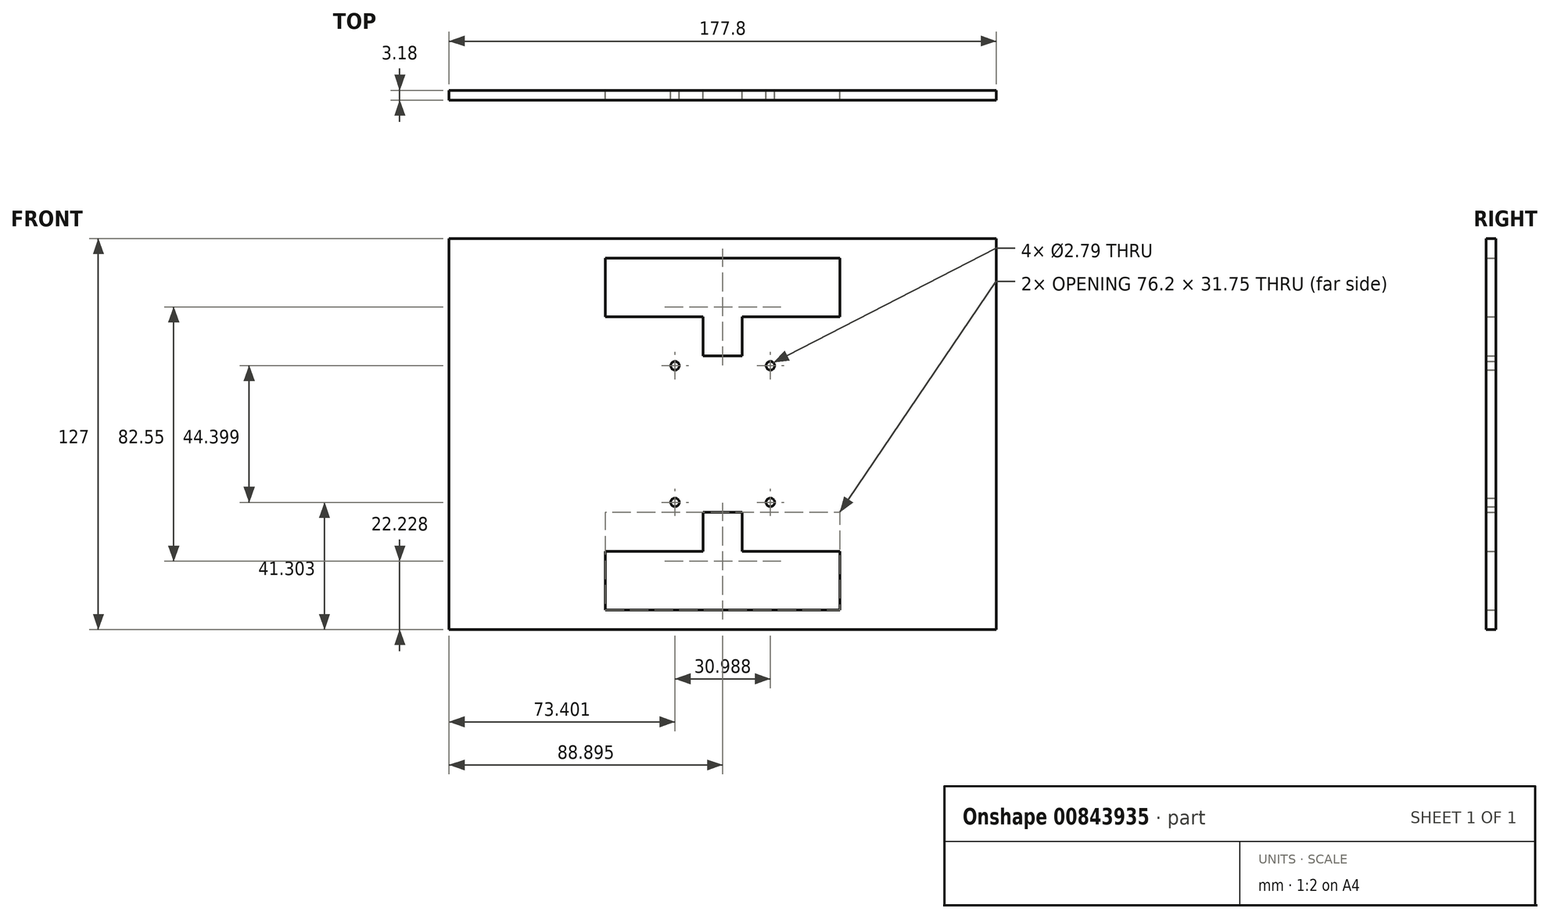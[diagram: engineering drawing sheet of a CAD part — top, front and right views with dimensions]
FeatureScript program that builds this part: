
annotation { "Feature Type Name" : "Feature", "Feature Type Description" : "" }
export const myFeature = defineFeature(function(context is Context, id is Id, definition is map)
    precondition{}
    {
        {
            var Q0;
            Q0=qCreatedBy(makeId("Front.planeOp"),FACE);
            var sketch = newSketch(context, id + "F0", { "sketchPlane" : qUnion([Q0])});
            skCircle(sketch, "E0", {"center": v(-17.23, 93.98) * mm, "radius": 1.4 * mm});
            skCircle(sketch, "E1", {"center": v(13.76, 93.98) * mm, "radius": 1.4 * mm});
            skCircle(sketch, "E2", {"center": v(-17.23, 49.58) * mm, "radius": 1.4 * mm});
            skCircle(sketch, "E3", {"center": v(13.76, 49.58) * mm, "radius": 1.4 * mm});
            skLineSegment(sketch, "E4.bottom", {"start": v(-39.83, 128.93) * mm, "end": v(36.37, 128.93) * mm});
            skLineSegment(sketch, "E4.top", {"start": v(-39.83, 109.88) * mm, "end": v(-8.08, 109.88) * mm});
            skLineSegment(sketch, "E4.left", {"start": v(-39.83, 128.93) * mm, "end": v(-39.83, 109.88) * mm});
            skLineSegment(sketch, "E4.right", {"start": v(36.37, 128.93) * mm, "end": v(36.37, 109.88) * mm});
            skLineSegment(sketch, "E5.bottom", {"start": v(-39.83, 33.68) * mm, "end": v(-8.08, 33.68) * mm});
            skLineSegment(sketch, "E5.top", {"start": v(-39.83, 14.63) * mm, "end": v(36.37, 14.63) * mm});
            skLineSegment(sketch, "E5.left", {"start": v(-39.83, 33.68) * mm, "end": v(-39.83, 14.63) * mm});
            skLineSegment(sketch, "E5.right", {"start": v(36.37, 33.68) * mm, "end": v(36.37, 14.63) * mm});
            skLineSegment(sketch, "E6", {"start": v(-8.08, 46.38) * mm, "end": v(-8.08, 33.68) * mm});
            skLineSegment(sketch, "E7", {"start": v(4.62, 46.38) * mm, "end": v(4.62, 33.68) * mm});
            skPoint(sketch, "E8.start.orphan", {"position": v(-16.98, 33.68) * mm});
            skLineSegment(sketch, "E9", {"start": v(-8.08, 109.88) * mm, "end": v(-8.08, 97.18) * mm});
            skLineSegment(sketch, "E10", {"start": v(-8.08, 97.18) * mm, "end": v(4.62, 97.18) * mm});
            skLineSegment(sketch, "E11", {"start": v(4.62, 97.18) * mm, "end": v(4.62, 109.88) * mm});
            skLineSegment(sketch, "E12.trimOffspring", {"start": v(4.62, 109.88) * mm, "end": v(36.37, 109.88) * mm});
            skLineSegment(sketch, "E13.trimOffspring", {"start": v(4.62, 33.68) * mm, "end": v(36.37, 33.68) * mm});
            skLineSegment(sketch, "E14", {"start": v(-8.08, 46.38) * mm, "end": v(4.62, 46.38) * mm});
            skLineSegment(sketch, "E15.bottom", {"start": v(-90.63, 135.28) * mm, "end": v(87.17, 135.28) * mm});
            skLineSegment(sketch, "E15.top", {"start": v(-90.63, 8.28) * mm, "end": v(87.17, 8.28) * mm});
            skLineSegment(sketch, "E15.left", {"start": v(-90.63, 135.28) * mm, "end": v(-90.63, 8.28) * mm});
            skLineSegment(sketch, "E15.right", {"start": v(87.17, 135.28) * mm, "end": v(87.17, 8.28) * mm});
            skSolve(sketch);
        }
        {
            var Q0;
            {var subQ9=sQuery(id+"F0.wireOp",EDGE,"8IdLV2Mn-u2Z9-jNTO-mBkL-c8aDUmhlKkYG.right");Q0=makeQuery(id+"F0.imprint","IMPRINT",FACE,{"disambiguationData":[TD([[makeQuery(id+"F0.imprint","IMPRINT",EDGE,{"derivedFrom":subQ9}),-1.0]])]});}
            var Q1;
            Q1=makeQuery(id+"F0.imprint","IMPRINT",FACE,{"disambiguationData":[TD([[makeQuery(id+"F0.imprint","IMPRINT",EDGE,{"derivedFrom":sQuery(id+"F0.wireOp",EDGE,"E0")}),-1.0]])]});
            extrude(context, id + "F1", {"entities" : qUnion([Q0, Q1]), "depth" : 3.17 * mm, "offsetDistance" : 25.4 * mm});
        }
    });
